# Revit family: DIVITYP015
name_source: partatom
category: Furniture
units: mm (PartAtom-declared; Revit-internal decimal feet)

## family parameters
Always vertical = Yes
Cut with Voids When Loaded = No
OmniClass Number = 23.40.20.00
OmniClass Title = General Furniture and Specialties
Render Appearance Source = Family Geometry
Room Calculation Point = No
Shared = No
Work Plane-Based = No

## types (1)
- DIVITYP015
    Cost = 33665 $
    Default Elevation = 0 mm  [stored 0 ft]
    Description = 1 x LAMINATE MOBILE WHITEBOARD 42H x 72W x 30D THREE WHEEL, 7 x Snap-In Data Plate w/6 Gang Face - Black, 2 x Black Duplex Outlet - Line 1, 2 x Black Duplex Outlet - Line 2, 1 x Black Duplex Outlet - Line 3, 2 x Black Duplex Outlet - Line 4 - Dedicated, 2 x 18 in. Electrical Jumper  (Panel To Panel), 1 x 21 in. Electrical Jumper  (Extended Panel To Panel), 1 x LH Receptacle Mounted Base Infeed - 72L - 8 Wire, 4 Circuit, 1 x DiVi LINEAR BASE RACEWAY SHROUD 3-WAY 90 DEGREES, 2 x DiVi LINEAR HARD PANEL-PWR-PERM MONO- 42H X 36W, 1 x DiVi LINEAR HARD PANEL-PWR-PERM MONO- 50H X 24W, 1 x DiVi LINEAR HARD PANEL-PWR-PERM MONO- 50H X 48W, 1 x DiVi LINEAR Hard PANEL -NPWR-PERM MONO- 50H X 36W, 1 x DiVi LINEAR QTR GLASS PANEL -NPWR- PERM MONO 50H X 36W, 3 x DIVI LINEAR BASE RACEWAY SHROUD END OF RUN, 1 x TBL, REC, 2mm, 24Dx72Wx29H, HAL, E SERIES GLD 2 STAGE, 1 x Rectangular - 2mm Edge - 24D x 42W, 2 x Rectangular - 2mm Edge - 24D x 48W, 2 x Rectangular - 2mm Edge - 24D x 72W, 1 x Rectangular - 2mm Edge - 30D x 72W, 1 x Freestanding O-Leg 27" X 30", 6 x Flat Plate, 4 x Regular Cantilever - Left Hand - 24D, 3 x Regular Cantilever - Right Hand - 24D, 1 x Regular Cantilever - Left Hand - 30D, 1 x Regular Cantilever - Right Hand - 30D, 3 x Cbx Full Depth Bbf Ped 24dx28hx16w, 1 x Cbx Full Depth Ff Ped 24dx28hx16w, 1 x Cbx Suspended Hat Modesty 12h For 72w (56 Actual), 1 x Cbx Single Door Tower Hinge Right 24dx27hx15w, 1 x Divi Clip Screen, Panel Top, 1/4" Glass, 8hx72w
    Exported From CET Designer = Yes
    Manufacturer = AIS
    Model = A-TWWB423072
    Show DIVITYP015 = Yes
    VisibilityIndex = 0

note: [stored X ft] marks values corroborated as IEEE doubles in the binary element streams (Revit-internal decimal feet)

## geometry (parser evidence)
native form markers: Sweep x3
no freeform markers — native parametric forms only
